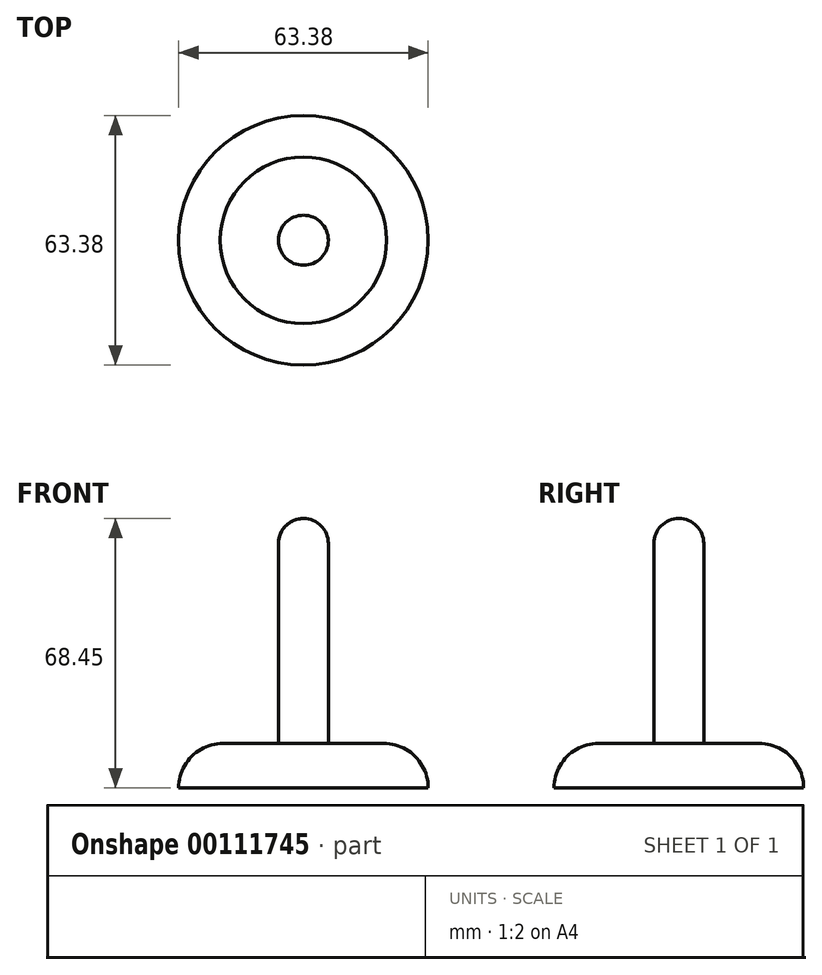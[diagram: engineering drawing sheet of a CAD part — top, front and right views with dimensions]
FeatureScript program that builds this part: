
annotation { "Feature Type Name" : "Feature", "Feature Type Description" : "" }
export const myFeature = defineFeature(function(context is Context, id is Id, definition is map)
    precondition{}
    {
        {
            var Q0;
            Q0=qCreatedBy(makeId("Front.planeOp"),FACE);
            var sketch = newSketch(context, id + "F0", { "sketchPlane" : qUnion([Q0])});
            skArc(sketch, "E0", {"start": v(0, 51.97) * mm, "mid": v(-4.5, 50.11) * mm, "end": v(-6.35, 45.62) * mm});
            skLineSegment(sketch, "E1", {"start": v(-6.35, 45.62) * mm, "end": v(-6.35, -5.18) * mm});
            skLineSegment(sketch, "E2.bottom", {"start": v(-6.35, -5.18) * mm, "end": v(-21.15, -5.18) * mm});
            skLineSegment(sketch, "E2.top", {"start": v(-6.35, -16.48) * mm, "end": v(-31.7, -16.48) * mm});
            skLineSegment(sketch, "E2.left", {"start": v(-6.35, -5.18) * mm, "end": v(-6.35, -16.48) * mm});
            skArc(sketch, "E3", {"start": v(-21.15, -5.18) * mm, "mid": v(-28.65, -8.75) * mm, "end": v(-31.7, -16.48) * mm});
            skLineSegment(sketch, "E4", {"start": v(0, 51.97) * mm, "end": v(0, 39.27) * mm});
            skPoint(sketch, "E5.start.orphan", {"position": v(6.35, 45.62) * mm});
            skLineSegment(sketch, "E6", {"start": v(-6.35, -16.48) * mm, "end": v(0, -16.48) * mm});
            skLineSegment(sketch, "E7", {"start": v(0, -16.48) * mm, "end": v(0, 39.27) * mm});
            skSolve(sketch);
        }
        {
            var Q0;
            Q0=makeQuery(id+"F0.imprint","IMPRINT",FACE,{"disambiguationData":[TD([[makeQuery(id+"F0.imprint","IMPRINT",EDGE,{"derivedFrom":sQuery(id+"F0.wireOp",EDGE,"E2.bottom")}),1.0]])]});
            var Q1;
            Q1=makeQuery(id+"F0.imprint","IMPRINT",FACE,{"disambiguationData":[TD([[makeQuery(id+"F0.imprint","IMPRINT",EDGE,{"derivedFrom":sQuery(id+"F0.wireOp",EDGE,"E0")}),1.0]])]});
            var Q2;
            Q2=sQuery(id+"F0.wireOp",EDGE,"E7");
            revolve(context, id + "F1", {"entities" : qUnion([Q0, Q1]), "axis" : qUnion([Q2]), "revolveType" : RevolveType.FULL});
        }
    });
